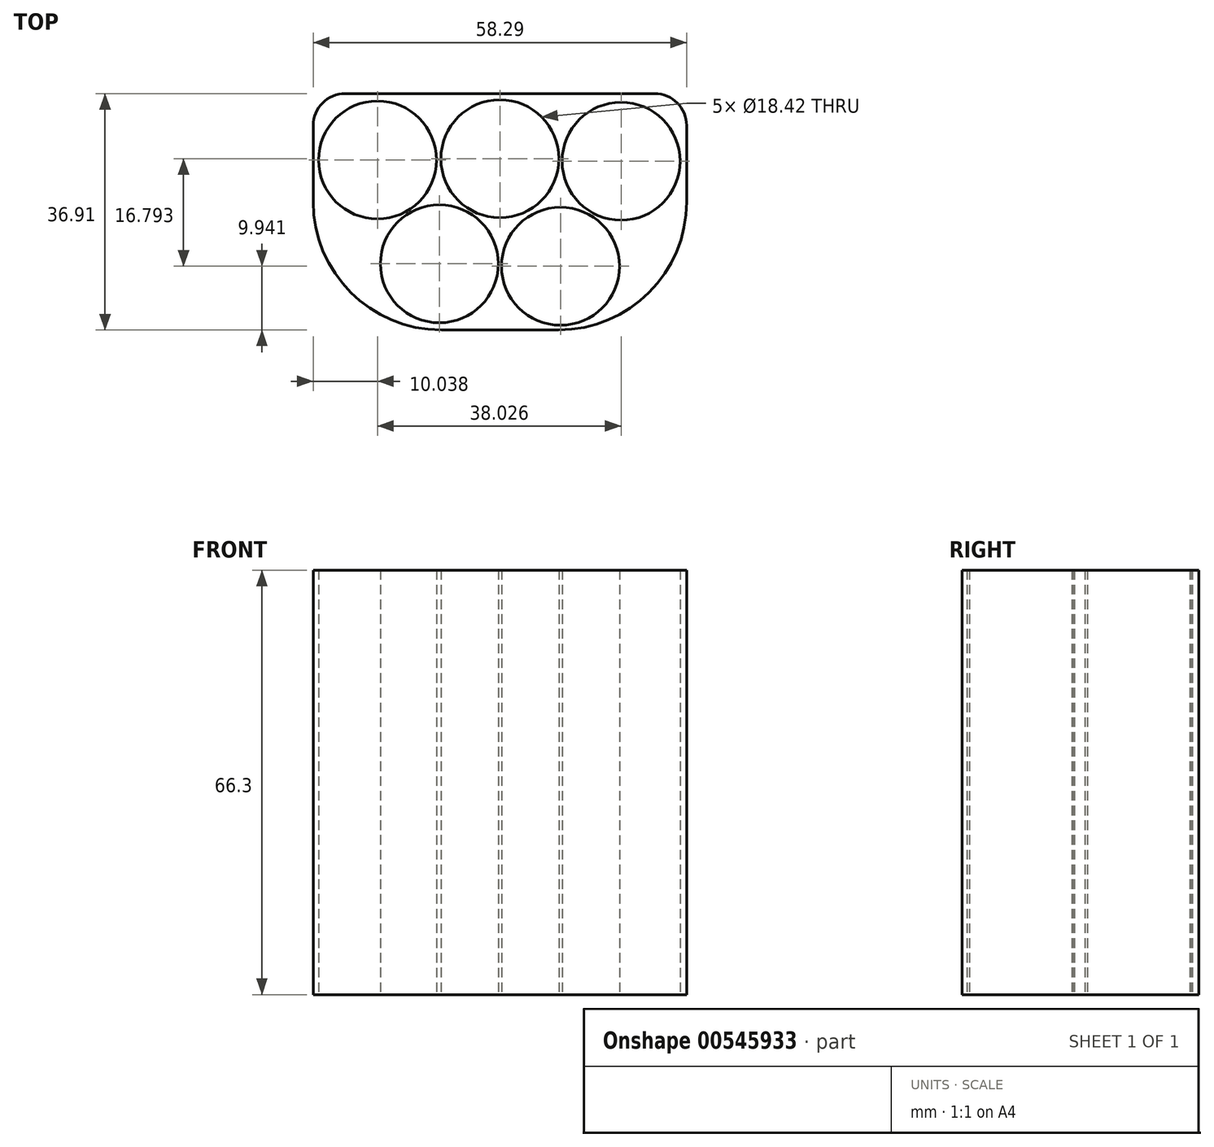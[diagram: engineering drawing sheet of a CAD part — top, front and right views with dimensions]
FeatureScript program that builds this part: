
annotation { "Feature Type Name" : "Feature", "Feature Type Description" : "" }
export const myFeature = defineFeature(function(context is Context, id is Id, definition is map)
    precondition{}
    {
        {
            var Q0;
            Q0=qCreatedBy(makeId("Top.planeOp"),FACE);
            var sketch = newSketch(context, id + "F0", { "sketchPlane" : qUnion([Q0])});
            skCircle(sketch, "E0", {"center": v(-34.55, 26.54) * mm, "radius": 9.2 * mm});
            skCircle(sketch, "E1", {"center": v(-15.44, 26.73) * mm, "radius": 9.2 * mm});
            skCircle(sketch, "E2", {"center": v(3.47, 26.35) * mm, "radius": 9.2 * mm});
            skCircle(sketch, "E3", {"center": v(-24.9, 10.33) * mm, "radius": 9.2 * mm});
            skCircle(sketch, "E4", {"center": v(-5.98, 9.94) * mm, "radius": 9.2 * mm});
            skLineSegment(sketch, "E5.bottom", {"start": v(-44.59, 36.9) * mm, "end": v(13.7, 36.9) * mm});
            skLineSegment(sketch, "E5.top", {"start": v(-24.59, 0) * mm, "end": v(-6.3, 0) * mm});
            skLineSegment(sketch, "E5.left", {"start": v(-44.59, 36.9) * mm, "end": v(-44.59, 20) * mm});
            skLineSegment(sketch, "E5.right", {"start": v(13.7, 36.9) * mm, "end": v(13.7, 20) * mm});
            skPoint(sketch, "E6.visualSharp", {"position": v(-44.59, 0) * mm});
            skArc(sketch, "E6.filletArc", {"start": v(-44.59, 20) * mm, "mid": v(-38.73, 5.86) * mm, "end": v(-24.59, 0) * mm});
            skPoint(sketch, "E7.visualSharp", {"position": v(13.7, 0) * mm});
            skArc(sketch, "E7.filletArc", {"start": v(-6.3, 0) * mm, "mid": v(7.85, 5.86) * mm, "end": v(13.7, 20) * mm});
            skSolve(sketch);
        }
        {
            var Q0;
            Q0=makeQuery(id+"F0.imprint","IMPRINT",FACE,{"disambiguationData":[TD([[makeQuery(id+"F0.imprint","IMPRINT",EDGE,{"derivedFrom":sQuery(id+"F0.wireOp",EDGE,"E0")}),-1.0]])]});
            extrude(context, id + "F1", {"entities" : qUnion([Q0]), "depth" : 66.3 * mm, "offsetDistance" : 25 * mm});
        }
        {
            var Q0;
            Q0=makeQuery(id+"F1.opExtrude","SWEPT_EDGE",EDGE,{"disambiguationData":[OSD([sQuery(id+"F0.wireOp",EDGE,"E5.bottom"),sQuery(id+"F0.wireOp",EDGE,"E5.right")])]});
            var Q1;
            Q1=makeQuery(id+"F1.opExtrude","SWEPT_EDGE",EDGE,{"disambiguationData":[OSD([sQuery(id+"F0.wireOp",EDGE,"E5.bottom"),sQuery(id+"F0.wireOp",EDGE,"E5.left")])]});
            fillet(context, id + "F2", {"entities" : qUnion([Q0, Q1]), "radius" : 5 * mm, "tangentPropagation" : true, "allowEdgeOverflow" : false});
        }
    });
